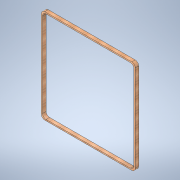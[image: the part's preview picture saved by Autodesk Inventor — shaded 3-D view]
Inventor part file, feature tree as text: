
AUTODESK INVENTOR PART (.ipt)
format: ipt  version: 2022 (Build 260153000, 153)  size: 124,416 bytes
history: native  units: in
note: dims shown in document units (in); Inventor stores cm internally (conversion verified against a paired STEP export)
features: helix x1, extrude x1, sketch x1
ambient origin geometry x8: Origin, YZ Plane, XZ Plane, XY Plane, X Axis, Y Axis, Z Axis, Center Point
bodies: Solid1 (feature_tree)
feature tree (3):
  helix  "Coil1or2"  [1 undecoded]
  extrude  "Extrusion1"  Depth=72.4409in
  sketch  "Sketch1"  dims[d1=74.4094in d2=72.4409in d3=72.4409in d4=2.7559in d5=0.0in d6=2.7559in]
note: 1 required parameter value undecoded (feature->parameter linkage not recoverable at this tier; creation-order binding heuristic only, values carry confidence <= 0.55)
